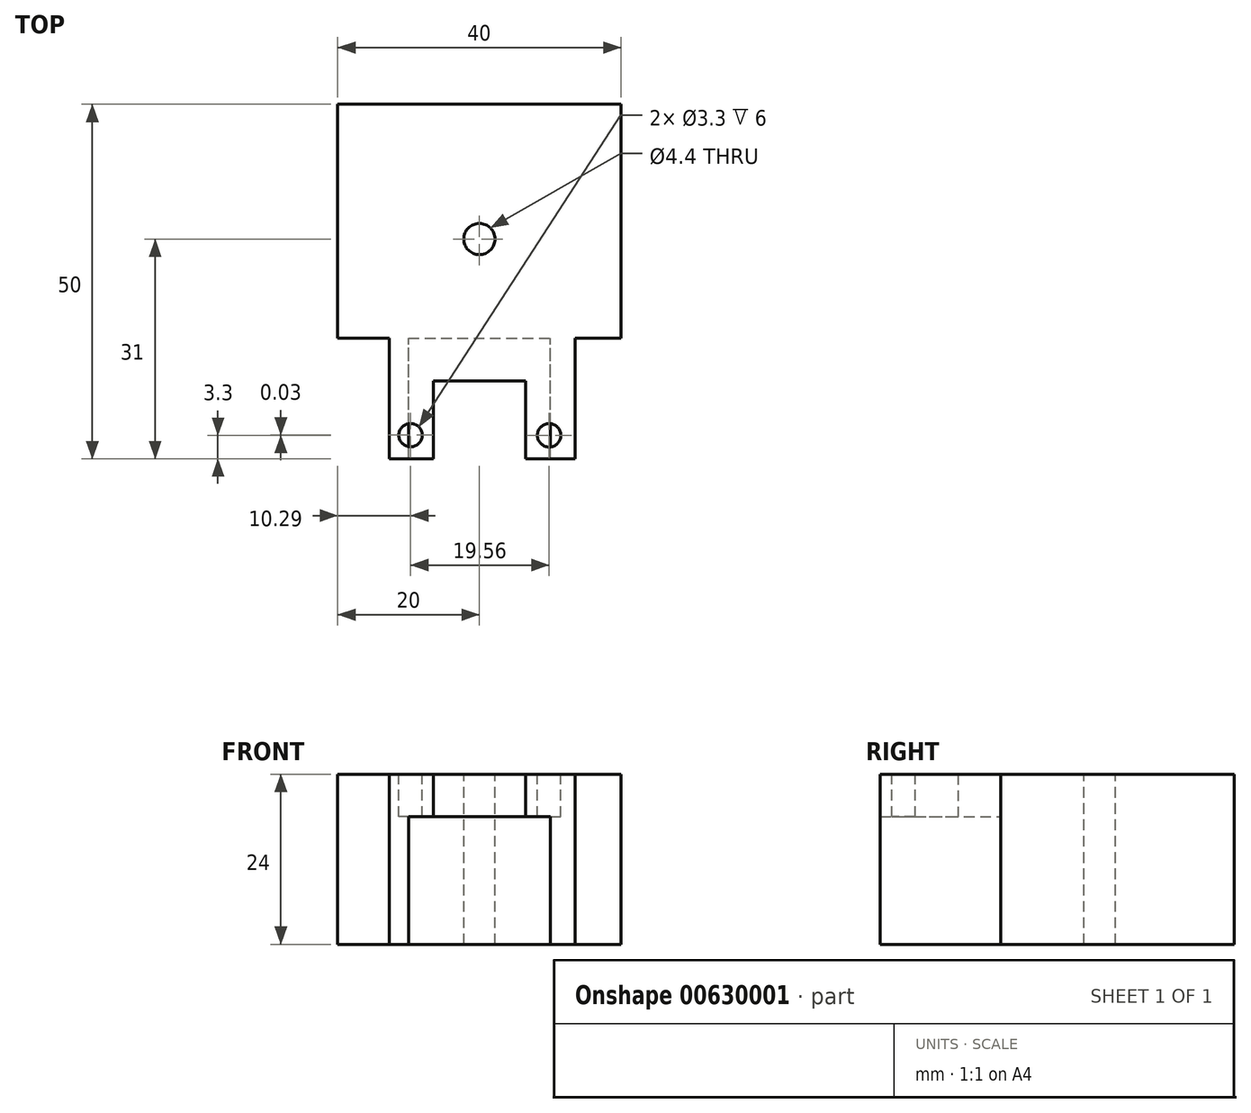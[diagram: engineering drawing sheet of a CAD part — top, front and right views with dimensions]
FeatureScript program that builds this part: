
annotation { "Feature Type Name" : "Feature", "Feature Type Description" : "" }
export const myFeature = defineFeature(function(context is Context, id is Id, definition is map)
    precondition{}
    {
        {
            var Q0;
            Q0=qCreatedBy(makeId("Top.planeOp"),FACE);
            var sketch = newSketch(context, id + "F0", { "sketchPlane" : qUnion([Q0])});
            skLineSegment(sketch, "E0.bottom", {"start": v(-20, 25) * mm, "end": v(20, 25) * mm});
            skLineSegment(sketch, "E0.top", {"start": v(-20, -25) * mm, "end": v(20, -25) * mm});
            skLineSegment(sketch, "E0.left", {"start": v(-20, 25) * mm, "end": v(-20, -25) * mm});
            skLineSegment(sketch, "E0.right", {"start": v(20, 25) * mm, "end": v(20, -25) * mm});
            skSolve(sketch);
        }
        {
            var Q0;
            Q0=makeQuery(id+"F0.imprint","IMPRINT",FACE,{"disambiguationData":[TD([[makeQuery(id+"F0.imprint","IMPRINT",EDGE,{"derivedFrom":sQuery(id+"F0.wireOp",EDGE,"E0.bottom")}),-1.0]])]});
            extrude(context, id + "F1", {"entities" : qUnion([Q0]), "depth" : 24 * mm, "offsetDistance" : 25 * mm});
        }
        {
            var Q0;
            Q0=makeQuery(id+"F1.opExtrude","CAP_FACE",FACE,{"disambiguationData":[OSD([sQuery(id+"F0.wireOp",EDGE,"E0.bottom"),sQuery(id+"F0.wireOp",EDGE,"E0.top"),sQuery(id+"F0.wireOp",EDGE,"E0.left"),sQuery(id+"F0.wireOp",EDGE,"E0.right")])],"isStart":false});
            var sketch = newSketch(context, id + "F2", { "sketchPlane" : qUnion([Q0])});
            skLineSegment(sketch, "E1.bottom", {"start": v(20, -25) * mm, "end": v(12.71, -25) * mm});
            skLineSegment(sketch, "E1.top", {"start": v(20, -8) * mm, "end": v(12.7, -8) * mm});
            skLineSegment(sketch, "E1.left", {"start": v(20, -25) * mm, "end": v(20, -8) * mm});
            skLineSegment(sketch, "E1.right", {"start": v(12.71, -25) * mm, "end": v(12.71, -8) * mm});
            skLineSegment(sketch, "E2.MirrorCS", {"start": v(-20, -8) * mm, "end": v(-12.7, -8) * mm});
            skLineSegment(sketch, "E3.MirrorCS", {"start": v(-12.71, -25) * mm, "end": v(-12.71, -8) * mm});
            skLineSegment(sketch, "E4.MirrorCS", {"start": v(-20, -25) * mm, "end": v(-12.71, -25) * mm});
            skLineSegment(sketch, "E5.MirrorCS", {"start": v(-20, -25) * mm, "end": v(-20, -8) * mm});
            skPoint(sketch, "E6", {"position": v(0, 16) * mm});
            skSolve(sketch);
        }
        {
            var Q0;
            Q0 = qSketchRegion(id + "F2", true);
            extrude(context, id + "F3", {"entities" : qUnion([Q0]), "operationType" : NewBodyOperationType.REMOVE, "oppositeDirection" : true, "depth" : 25 * mm, "offsetDistance" : 25 * mm});
        }
        {
            var Q0;
            Q0=makeQuery(id+"F1.opExtrude","CAP_FACE",FACE,{"disambiguationData":[OSD([sQuery(id+"F0.wireOp",EDGE,"E0.bottom"),sQuery(id+"F0.wireOp",EDGE,"E0.top"),sQuery(id+"F0.wireOp",EDGE,"E0.left"),sQuery(id+"F0.wireOp",EDGE,"E0.right")])],"isStart":true});
            var sketch = newSketch(context, id + "F4", { "sketchPlane" : qUnion([Q0])});
            skLineSegment(sketch, "E7.bottom", {"start": v(-10, 25) * mm, "end": v(10, 25) * mm});
            skLineSegment(sketch, "E7.top", {"start": v(-10, -25) * mm, "end": v(10, -25) * mm});
            skLineSegment(sketch, "E7.left", {"start": v(-10, 25) * mm, "end": v(-10, -25) * mm});
            skLineSegment(sketch, "E7.right", {"start": v(10, 25) * mm, "end": v(10, -25) * mm});
            skSolve(sketch);
        }
        {
            var Q0;
            Q0 = qSketchRegion(id + "F4", true);
            extrude(context, id + "F5", {"entities" : qUnion([Q0]), "operationType" : NewBodyOperationType.REMOVE, "oppositeDirection" : true, "depth" : 3 * mm, "offsetDistance" : 25 * mm});
        }
        {
            var Q0;
            Q0=makeQuery(id+"F5.boolean.opBoolean","COPY",FACE,{"derivedFrom":makeQuery(id+"F5.opExtrude","CAP_FACE",FACE,{"disambiguationData":[OSD([sQuery(id+"F4.wireOp",EDGE,"E7.bottom"),sQuery(id+"F4.wireOp",EDGE,"E7.top"),sQuery(id+"F4.wireOp",EDGE,"E7.left"),sQuery(id+"F4.wireOp",EDGE,"E7.right")])],"isStart":false})});
            var sketch = newSketch(context, id + "F6", { "sketchPlane" : qUnion([Q0])});
            skLineSegment(sketch, "E8.bottom", {"start": v(6.5, 25) * mm, "end": v(-6.5, 25) * mm});
            skLineSegment(sketch, "E8.top", {"start": v(6.5, 14) * mm, "end": v(-6.5, 14) * mm});
            skLineSegment(sketch, "E8.left", {"start": v(6.5, 25) * mm, "end": v(6.5, 14) * mm});
            skLineSegment(sketch, "E8.right", {"start": v(-6.5, 25) * mm, "end": v(-6.5, 14) * mm});
            skSolve(sketch);
        }
        {
            var Q0;
            Q0 = qSketchRegion(id + "F6", true);
            extrude(context, id + "F7", {"entities" : qUnion([Q0]), "operationType" : NewBodyOperationType.REMOVE, "oppositeDirection" : true, "depth" : 6 * mm, "offsetDistance" : 25 * mm});
        }
        {
            var Q0;
            Q0=makeQuery(id+"F1.opExtrude","SWEPT_FACE",FACE,{"disambiguationData":[OSD([sQuery(id+"F0.wireOp",EDGE,"E0.top")])]});
            var sketch = newSketch(context, id + "F8", { "sketchPlane" : qUnion([Q0])});
            skPoint(sketch, "E9.firstSnap0", {"position": v(12.71, 12) * mm});
            skLineSegment(sketch, "E10.bottom", {"start": v(20, 24) * mm, "end": v(-20, 24) * mm});
            skLineSegment(sketch, "E10.top", {"start": v(20, 9) * mm, "end": v(-20, 9) * mm});
            skLineSegment(sketch, "E10.left", {"start": v(20, 24) * mm, "end": v(20, 9) * mm});
            skLineSegment(sketch, "E10.right", {"start": v(-20, 24) * mm, "end": v(-20, 9) * mm});
            skSolve(sketch);
        }
        {
            var Q0;
            Q0 = qSketchRegion(id + "F8", true);
            var Q1;
            Q1=makeQuery(id+"F1.opExtrude","SWEPT_FACE",FACE,{"disambiguationData":[OSD([sQuery(id+"F0.wireOp",EDGE,"E0.bottom")])]});
            extrude(context, id + "F9", {"entities" : qUnion([Q0]), "operationType" : NewBodyOperationType.REMOVE, "endBound" : BoundingType.UP_TO_SURFACE, "oppositeDirection" : true, "depth" : 25 * mm, "endBoundEntityFace" : qUnion([Q1]), "offsetDistance" : 25 * mm});
        }
        {
            var Q0;
            {var subQ0=sQuery(id+"F0.wireOp",EDGE,"E0.top");var subQ1=sQuery(id+"F0.wireOp",EDGE,"E0.right");var subQ2=sQuery(id+"F0.wireOp",EDGE,"E0.bottom");Q0=makeQuery(id+"F5.boolean.opBoolean","SPLIT",FACE,{"disambiguationData":[TD([makeQuery(id+"F1.opExtrude","SWEPT_FACE",FACE,{"disambiguationData":[OSD([subQ1])]})])],"derivedFrom":makeQuery(id+"F1.opExtrude","CAP_FACE",FACE,{"disambiguationData":[OSD([subQ2,subQ0,sQuery(id+"F0.wireOp",EDGE,"E0.left"),subQ1])],"isStart":true})});}
            var Q1;
            {var subQ0=sQuery(id+"F0.wireOp",EDGE,"E0.bottom");var subQ1=sQuery(id+"F0.wireOp",EDGE,"E0.left");var subQ2=sQuery(id+"F0.wireOp",EDGE,"E0.top");Q1=makeQuery(id+"F5.boolean.opBoolean","SPLIT",FACE,{"disambiguationData":[TD([makeQuery(id+"F1.opExtrude","SWEPT_FACE",FACE,{"disambiguationData":[OSD([subQ1])]})])],"derivedFrom":makeQuery(id+"F1.opExtrude","CAP_FACE",FACE,{"disambiguationData":[OSD([subQ0,subQ2,subQ1,sQuery(id+"F0.wireOp",EDGE,"E0.right")])],"isStart":true})});}
            extrude(context, id + "F10", {"entities" : qUnion([Q0, Q1]), "operationType" : NewBodyOperationType.ADD, "depth" : 15 * mm, "offsetDistance" : 25 * mm});
        }
        {
            var Q0;
            {var subQ0=sQuery(id+"F0.wireOp",EDGE,"E0.bottom");var subQ1=makeQuery(id+"F1.opExtrude","SWEPT_FACE",FACE,{"disambiguationData":[OSD([subQ0])]});var subQ2=sQuery(id+"F0.wireOp",EDGE,"E0.right");var subQ3=sQuery(id+"F0.wireOp",EDGE,"E0.left");var subQ5=makeQuery(id+"F1.opExtrude","CAP_EDGE",EDGE,{"disambiguationData":[OSD([subQ0])],"isStart":true});Q0=makeQuery(id+"F10.boolean.opBoolean","MERGE",FACE,{"derivedFrom":[subQ1,makeQuery(id+"F10.opExtrude","SWEPT_FACE",FACE,{"disambiguationData":[OSD([subQ0]),TDD([makeQuery(id+"F5.boolean.opBoolean","SPLIT",EDGE,{"disambiguationData":[TD([makeQuery(id+"F1.opExtrude","SWEPT_FACE",FACE,{"disambiguationData":[OSD([subQ3])]})])],"derivedFrom":subQ5})])]}),makeQuery(id+"F10.opExtrude","SWEPT_FACE",FACE,{"disambiguationData":[OSD([subQ0]),TDD([makeQuery(id+"F5.boolean.opBoolean","SPLIT",EDGE,{"disambiguationData":[TD([makeQuery(id+"F1.opExtrude","SWEPT_FACE",FACE,{"disambiguationData":[OSD([subQ2])]})])],"derivedFrom":subQ5})])]})]});}
            var sketch = newSketch(context, id + "F11", { "sketchPlane" : qUnion([Q0])});
            skLineSegment(sketch, "E11.bottom", {"start": v(-10, -15) * mm, "end": v(10, -15) * mm});
            skLineSegment(sketch, "E11.top", {"start": v(-10, 3) * mm, "end": v(10, 3) * mm});
            skLineSegment(sketch, "E11.left", {"start": v(-10, -15) * mm, "end": v(-10, 3) * mm});
            skLineSegment(sketch, "E11.right", {"start": v(10, -15) * mm, "end": v(10, 3) * mm});
            skSolve(sketch);
        }
        {
            var Q0;
            Q0=makeQuery(id+"F11.imprint","IMPRINT",FACE,{"disambiguationData":[TD([[makeQuery(id+"F11.imprint","IMPRINT",EDGE,{"derivedFrom":sQuery(id+"F11.wireOp",EDGE,"E11.bottom")}),1.0]])]});
            extrude(context, id + "F12", {"entities" : qUnion([Q0]), "operationType" : NewBodyOperationType.ADD, "oppositeDirection" : true, "depth" : 33 * mm, "offsetDistance" : 25 * mm});
        }
        {
            var Q0;
            {var subQ0=sQuery(id+"F2.wireOp",EDGE,"E1.right");Q0=makeQuery(id+"F10.boolean.opBoolean","MERGE",FACE,{"derivedFrom":[makeQuery(id+"F3.boolean.opBoolean","COPY",FACE,{"derivedFrom":makeQuery(id+"F3.opExtrude","SWEPT_FACE",FACE,{"disambiguationData":[OSD([subQ0])]})}),makeQuery(id+"F10.opExtrude","SWEPT_FACE",FACE,{"disambiguationData":[OSD([sQuery(id+"F0.wireOp",EDGE,"E0.bottom"),sQuery(id+"F0.wireOp",EDGE,"E0.top"),sQuery(id+"F0.wireOp",EDGE,"E0.left"),sQuery(id+"F0.wireOp",EDGE,"E0.right"),subQ0])]})]});}
            extrude(context, id + "F13", {"entities" : qUnion([Q0]), "operationType" : NewBodyOperationType.ADD, "depth" : 0.8 * mm, "offsetDistance" : 25 * mm});
        }
        {
            var Q0;
            {var subQ0=sQuery(id+"F8.wireOp",EDGE,"E10.top");Q0=makeQuery(id+"F13.boolean.opBoolean","MERGE",FACE,{"derivedFrom":[makeQuery(id+"F9.boolean.opBoolean","COPY",FACE,{"derivedFrom":makeQuery(id+"F9.opExtrude","SWEPT_FACE",FACE,{"disambiguationData":[OSD([subQ0])]})}),makeQuery(id+"F13.opExtrude","SWEPT_FACE",FACE,{"disambiguationData":[OSD([sQuery(id+"F2.wireOp",EDGE,"E1.right"),subQ0])]})]});}
            var sketch = newSketch(context, id + "F14", { "sketchPlane" : qUnion([Q0])});
            skPoint(sketch, "E12", {"position": v(9.85, -21.7) * mm});
            skPoint(sketch, "E13", {"position": v(-9.7, -21.67) * mm});
            skCircle(sketch, "E14", {"center": v(-9.7, -21.67) * mm, "radius": 1.65 * mm});
            skCircle(sketch, "E15", {"center": v(9.85, -21.7) * mm, "radius": 1.65 * mm});
            skSolve(sketch);
        }
        {
            var Q0;
            {var subQ0=sQuery(id+"F8.wireOp",EDGE,"E10.top");Q0=makeQuery(id+"F13.boolean.opBoolean","MERGE",FACE,{"derivedFrom":[makeQuery(id+"F9.boolean.opBoolean","COPY",FACE,{"derivedFrom":makeQuery(id+"F9.opExtrude","SWEPT_FACE",FACE,{"disambiguationData":[OSD([subQ0])]})}),makeQuery(id+"F13.opExtrude","SWEPT_FACE",FACE,{"disambiguationData":[OSD([sQuery(id+"F2.wireOp",EDGE,"E1.right"),subQ0])]})]});}
            var sketch = newSketch(context, id + "F15", { "sketchPlane" : qUnion([Q0])});
            skPoint(sketch, "E16", {"position": v(0, 6) * mm});
            skSolve(sketch);
        }
        {
            var Q0;
            Q0=sQuery(id+"F15.wireOp",VERTEX,"E16");
            var Q1;
            Q1=makeQuery(id+"F1.opExtrude","SWEPT_BODY",BODY,{"disambiguationData":[OSD([sQuery(id+"F0.wireOp",EDGE,"E0.bottom"),sQuery(id+"F0.wireOp",EDGE,"E0.top"),sQuery(id+"F0.wireOp",EDGE,"E0.left"),sQuery(id+"F0.wireOp",EDGE,"E0.right")])]});
            hole(context, id + "F16", {"style" : HoleStyle.SIMPLE, "endStyle" : HoleEndStyle.THROUGH, "standardTappedOrClearance" : lookupTablePath({ "standard" : "ISO", "fit" : "Normal", "size" : "M4", "type" : "Clearance" }), "standardBlindInLast" : lookupTablePath({ "fit" : "Standard", "standard" : "ISO", "size" : "M4", "type" : "Clearance" }), "holeDiameter" : 4.4 * mm, "majorDiameter" : 5 * mm, "isTappedThrough" : true, "tappedDepth" : 12 * mm, "tapClearance" : 3, "locations" : qUnion([Q0]), "scope" : qUnion([Q1])});
        }
        {
            var Q0;
            Q0 = qSketchRegion(id + "F14", true);
            extrude(context, id + "F17", {"entities" : qUnion([Q0]), "operationType" : NewBodyOperationType.REMOVE, "oppositeDirection" : true, "depth" : 6 * mm, "offsetDistance" : 25 * mm});
        }
    });
